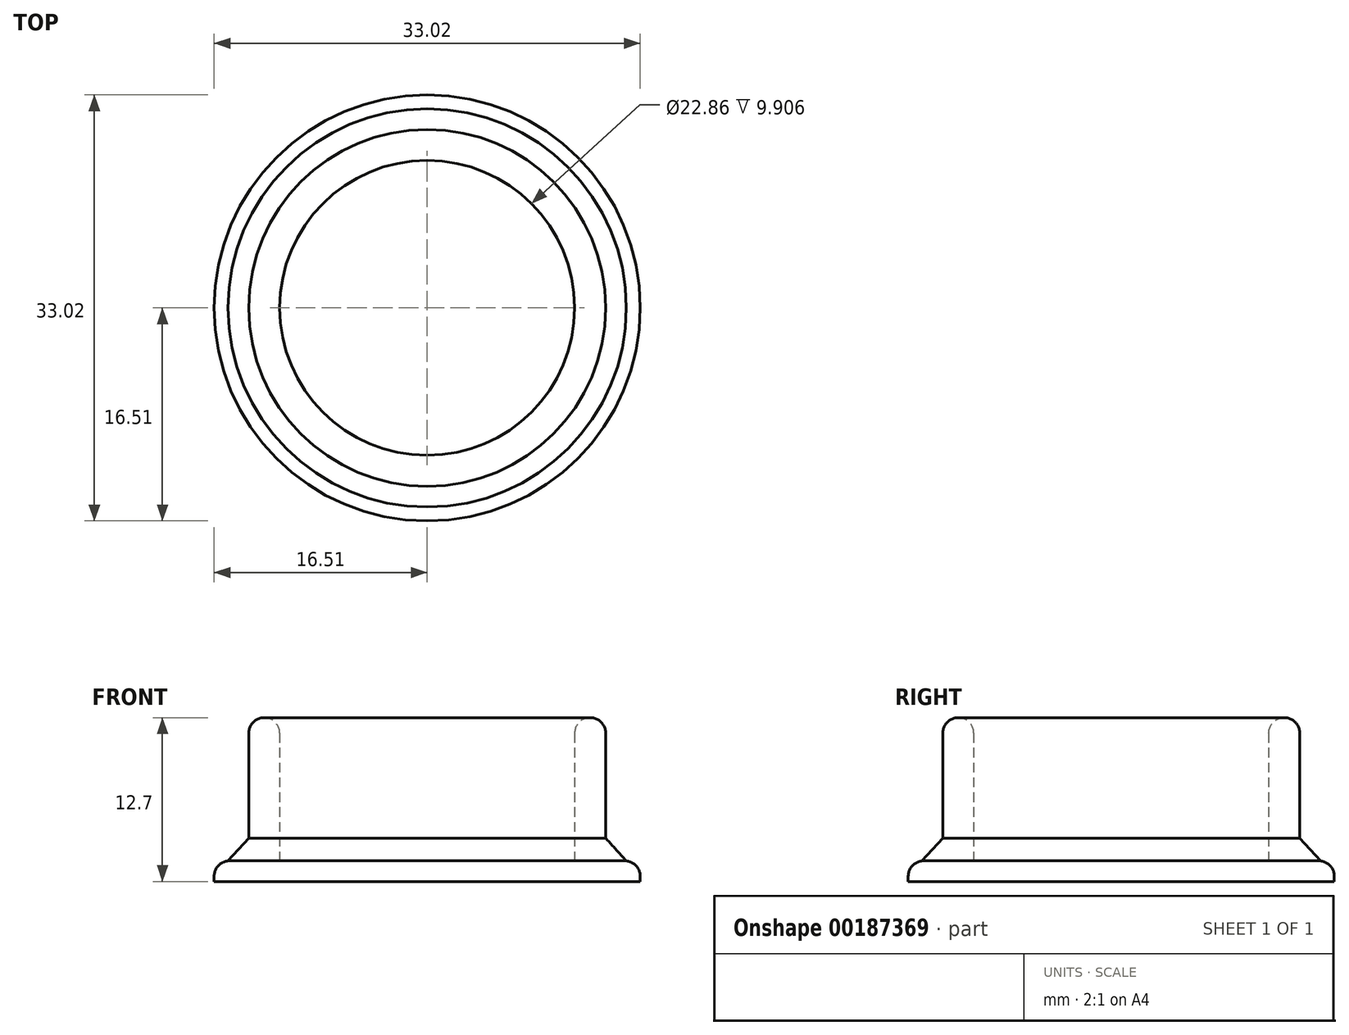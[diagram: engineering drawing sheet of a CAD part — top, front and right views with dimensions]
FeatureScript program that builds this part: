
annotation { "Feature Type Name" : "Feature", "Feature Type Description" : "" }
export const myFeature = defineFeature(function(context is Context, id is Id, definition is map)
    precondition{}
    {
        {
            var Q0;
            Q0=qCreatedBy(makeId("Top.planeOp"),FACE);
            var sketch = newSketch(context, id + "F0", { "sketchPlane" : qUnion([Q0])});
            skCircle(sketch, "E0", {"center": v(0, 0) * mm, "radius": 11.43 * mm});
            skCircle(sketch, "E1", {"center": v(0, 0) * mm, "radius": 13.83 * mm});
            skSolve(sketch);
        }
        {
            var Q0;
            Q0 = qSketchRegion(id + "F0", true);
            extrude(context, id + "F1", {"entities" : qUnion([Q0]), "depth" : 12.7 * mm});
        }
        {
            var Q0;
            Q0=qCreatedBy(makeId("Top.planeOp"),FACE);
            var sketch = newSketch(context, id + "F2", { "sketchPlane" : qUnion([Q0])});
            skCircle(sketch, "E2", {"center": v(0, 0) * mm, "radius": 16.51 * mm});
            skSolve(sketch);
        }
        {
            var Q0;
            Q0 = qSketchRegion(id + "F2", true);
            extrude(context, id + "F3", {"entities" : qUnion([Q0]), "operationType" : NewBodyOperationType.ADD, "depth" : 1.6 * mm});
        }
        {
            var Q0;
            Q0=makeQuery(id+"F3.opExtrude","CAP_EDGE",EDGE,{"disambiguationData":[OSD([sQuery(id+"F2.wireOp",EDGE,"E2")])],"isStart":false});
            var Q1;
            Q1=makeQuery(id+"F1.opExtrude","CAP_EDGE",EDGE,{"disambiguationData":[OSD([sQuery(id+"F0.wireOp",EDGE,"E1")])],"isStart":false});
            var Q2;
            Q2=makeQuery(id+"F1.opExtrude","CAP_EDGE",EDGE,{"disambiguationData":[OSD([sQuery(id+"F0.wireOp",EDGE,"E0")])],"isStart":false});
            fillet(context, id + "F4", {"entities" : qUnion([Q0, Q1, Q2]), "radius" : 1.2 * mm, "tangentPropagation" : true, "allowEdgeOverflow" : false});
        }
        {
            var Q0;
            Q0=makeQuery(id+"F3.boolean.opBoolean","INTERSECT",EDGE,{"derivedFrom":[makeQuery(id+"F1.opExtrude","SWEPT_FACE",FACE,{"disambiguationData":[OSD([sQuery(id+"F0.wireOp",EDGE,"E1")])]}),makeQuery(id+"F3.opExtrude","CAP_FACE",FACE,{"disambiguationData":[OSD([sQuery(id+"F2.wireOp",EDGE,"E2")])],"isStart":false})]});
            chamfer(context, id + "F5", {"entities" : qUnion([Q0]), "width" : 1.78 * mm, "tangentPropagation" : true});
        }
    });
